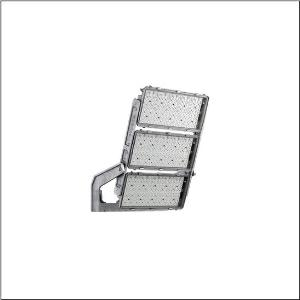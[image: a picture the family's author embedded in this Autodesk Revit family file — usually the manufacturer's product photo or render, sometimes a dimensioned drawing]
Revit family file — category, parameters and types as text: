
# Revit family: floodlight_fl_11_maxi_pro_remote___pl64blc_5xa779428w01aa_23f9
name_source: partatom
category: Lighting Fixtures
units: mm (PartAtom-declared; Revit-internal decimal feet)

## family parameters
Cut with Voids When Loaded = No
Host = Face
Light Source = No
Part Type = Normal
Room Calculation Point = No
Round Connector Dimension = Use Diameter
Shared = No

## types (1)
- --- (1 x LED, 127830 lm, 1516.9 W, 5700K)
    Apparent Load = 1517 VA
    CIE Flux Codes = 28 83 99 100 100
    Color Rendering = 80
    Color Temperature = 5700K
    Default Elevation = 1800 mm
    Description = Floodlight FL 11  maxi  pro Remote floodlight; light control with lens of PMMA; cover panel of toughened safety glass, transparent; light distribution: PL64BLC, asymmetric direct distribution, LEDcolour temperature: 5700K, rated luminous flux: 127.830lm, colour rendering: CRI > 80, light colour: 857; luminous efficacy: 84lm/W; brightness control: DALI 2 (1 DALI address); with terminal, 8-pole, max. 2.5mm², mains connection: 220..240V/380..400V AC, 50/60Hz, surge voltage resistance: line to ground: 10kV, dimming range 10..100%, dustproof LED module, LED unit replaceable without ESD environment, no afterglow with DALI off / DMX off command, ECG replaceable separately; 1517W floodlight with 3x LED unit of diecast aluminium, coated grey; length: 1.003mm / width: 651mm / height: 338mm; mounting bracket, of diecast aluminium, uncoated, natural, equipment: Power, protection rating (complete): IP66; insulation class (complete): insulation class I (protective earthing); certification: CE, ENEC, VDE; ball protection: ball impact resistant, impact resistance: IK07; only for outdoor installations, rated ambient temperature 10°C, permissible operating ambient temperature: -40..+30°C, permissible storage temperature: -40..+85°C; packaging unit: 1 piece

Light Distribution: PL64BLC
    Height = 320 mm
    Lamp = 1 x LED
    Lamp Light Flux = 127830 lm
    Lamp Power = 1516.9 W
    Lamp count = 1
    Length = 1002 mm
    Luminous efficacy = 84 lm/W
    Manufacturer = Siteco
    ModVariant = No
    Model = 5XA779428W01AA
    Mounting Place = Ceiling
    Mounting Type = Surface mounted
    Number of Poles = 1
    OnlyDefault = Yes
    Power Factor = 1
    Product Name = Floodlight FL 11 maxi pro Remote | PL64BLC
    Product group = floodlight | ceiling mounted
    ProductGroupID = 302
    Protection Class = Protection class I
    Protection Degree = IP 66
    RLX_Detail_Level = 1
    RLX_Emergency_Light_Flux = 0 lm
    RLX_Emergency_Type = 0
    RLX_Emergency_Type_DB = No
    RlxData = <blob elided: 52245 chars, md5=0b0a01c2>
    Socket = socket
    Standby Power = 0 W
    System Light Flux = 127830 lm
    System Power = 1517 W
    Type Comments = factory setting: luminous flux: 100 % | dim-lin: 254 | 1070 mA
    Type Image = l_1006784.jpg
    URL = http://relux.com
    VarID = @adj_049427
    Voltage = 0 V
    Weight = 0.00 kg
    Width = 655 mm

## geometry (parser evidence)
native form markers: Blend x4, Sweep x13
no freeform markers — native parametric forms only
